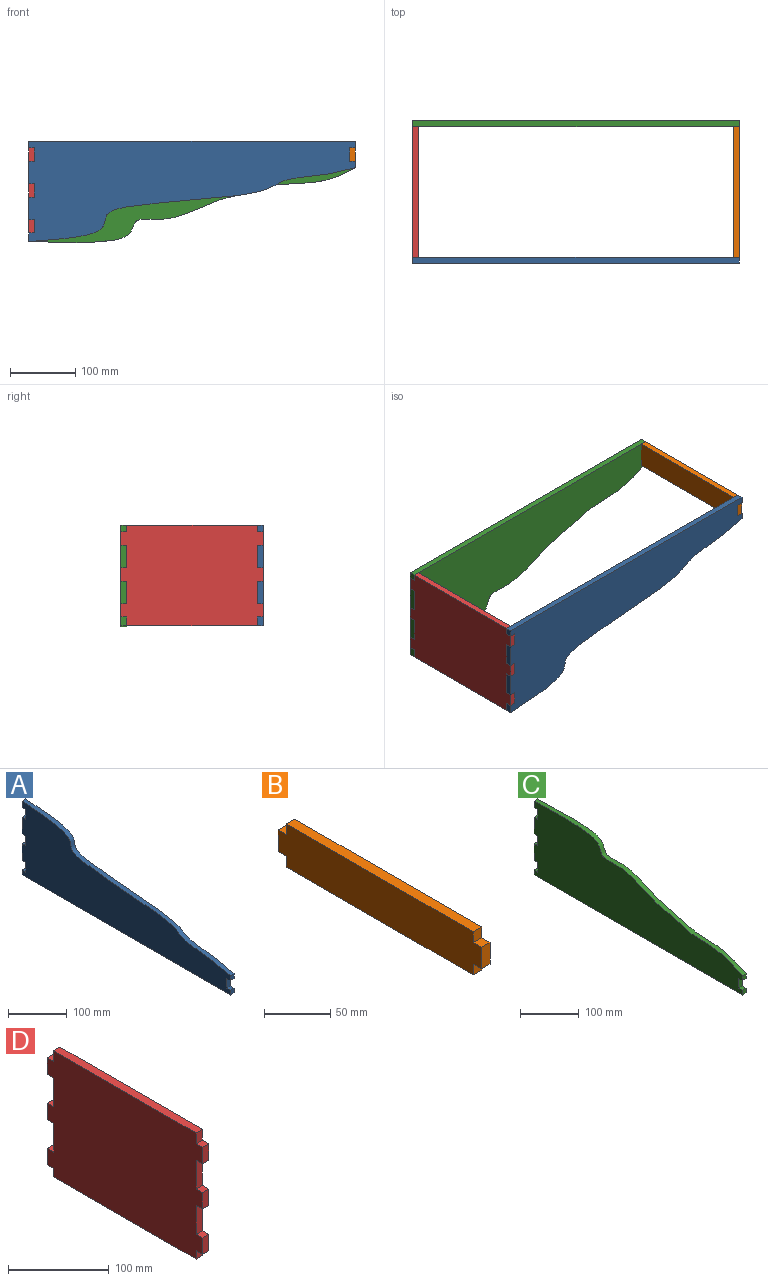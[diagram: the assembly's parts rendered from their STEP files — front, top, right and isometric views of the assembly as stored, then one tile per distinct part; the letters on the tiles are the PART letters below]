
ASSEMBLY  parts=4 mates=3
PART A: 22 faces, bbox 9x500x153.2 mm
  f0: plane 10x9mm, normal (0,1,0), area 90mm2, adj f1,f19,f20,f21
  f1: plane 9x9mm, normal (0,0,1), area 81mm2, adj f0,f2,f20,f21
  f2: plane 20x9mm, normal (0,1,0), area 180mm2, adj f1,f3,f20,f21
  f3: plane 9x9mm, normal (0,0,-1), area 81mm2, adj f2,f4,f20,f21
  f4: plane 35x9mm, normal (0,1,0), area 315mm2, adj f3,f5,f20,f21
  f5: plane 9x9mm, normal (0,0,1), area 81mm2, adj f4,f6,f20,f21
  f6: plane 20x9mm, normal (0,1,0), area 180mm2, adj f5,f7,f20,f21
  f7: plane 9x9mm, normal (0,0,-1), area 81mm2, adj f6,f8,f20,f21
  f8: plane 35x9mm, normal (0,1,0), area 315mm2, adj f7,f9,f20,f21
  f9: plane 9x9mm, normal (0,0,1), area 81mm2, adj f8,f10,f20,f21
  f10: plane 20x9mm, normal (0,1,0), area 180mm2, adj f9,f11,f20,f21
  f11: plane 9x9mm, normal (0,0,-1), area 81mm2, adj f10,f12,f20,f21
  f12: plane 13.18x9mm, normal (0,1,0), area 118.6mm2, adj f11,f13,f20,f21
  f13: extruded ~500x113.18mm, area 4761mm2, adj f12,f14,f20,f21
  f14: plane 10x9mm, normal (0,-1,0), area 90mm2, adj f13,f15,f20,f21
  f15: plane 9x9mm, normal (0,0,-1), area 81mm2, adj f14,f16,f20,f21
  f16: plane 20x9mm, normal (0,-1,0), area 180mm2, adj f15,f17,f20,f21
  f17: plane 9x9mm, normal (0,0,1), area 81mm2, adj f16,f18,f20,f21
  f18: plane 10x9mm, normal (0,-1,0), area 90mm2, adj f17,f19,f20,f21
  f19: plane 500x9mm, normal (0,0,-1), area 4500mm2, adj f0,f18,f20,f21
  f20: plane 500x153.18mm, normal (1,0,0), area 46145.7mm2, adj f0,f1,f2,f3,f4,f5,f6,f7
  f21: plane 500x153.18mm, normal (-1,0,0), area 46145.7mm2, adj f0,f1,f2,f3,f4,f5,f6,f7
PART B: 14 faces, bbox 9x218x40 mm
  f0: plane 9x9mm, normal (0,0,1), area 81mm2, adj f1,f11,f12,f13
  f1: plane 10x9mm, normal (0,1,0), area 90mm2, adj f0,f2,f12,f13
  f2: plane 200x9mm, normal (0,0,1), area 1800mm2, adj f1,f3,f12,f13
  f3: plane 10x9mm, normal (0,-1,0), area 90mm2, adj f2,f4,f12,f13
  f4: plane 9x9mm, normal (0,0,1), area 81mm2, adj f3,f5,f12,f13
  f5: plane 20x9mm, normal (0,-1,0), area 180mm2, adj f4,f6,f12,f13
  f6: plane 9x9mm, normal (0,0,-1), area 81mm2, adj f5,f7,f12,f13
  f7: plane 10x9mm, normal (0,-1,0), area 90mm2, adj f6,f8,f12,f13
  f8: plane 200x9mm, normal (0,0,-1), area 1800mm2, adj f7,f9,f12,f13
  f9: plane 10x9mm, normal (0,1,0), area 90mm2, adj f8,f10,f12,f13
  f10: plane 9x9mm, normal (0,0,-1), area 81mm2, adj f9,f11,f12,f13
  f11: plane 20x9mm, normal (0,1,0), area 180mm2, adj f0,f10,f12,f13
  f12: plane 218x40mm, normal (1,0,0), area 8360mm2, adj f0,f1,f2,f3,f4,f5,f6,f7
  f13: plane 218x40mm, normal (-1,0,0), area 8360mm2, adj f0,f1,f2,f3,f4,f5,f6,f7
PART C: 22 faces, bbox 9x500x159.2 mm
  f0: plane 10x9mm, normal (0,1,0), area 90mm2, adj f1,f19,f20,f21
  f1: plane 9x9mm, normal (0,0,1), area 81mm2, adj f0,f2,f20,f21
  f2: plane 20x9mm, normal (0,1,0), area 180mm2, adj f1,f3,f20,f21
  f3: plane 9x9mm, normal (0,0,-1), area 81mm2, adj f2,f4,f20,f21
  f4: plane 35x9mm, normal (0,1,0), area 315mm2, adj f3,f5,f20,f21
  f5: plane 9x9mm, normal (0,0,1), area 81mm2, adj f4,f6,f20,f21
  f6: plane 20x9mm, normal (0,1,0), area 180mm2, adj f5,f7,f20,f21
  f7: plane 9x9mm, normal (0,0,-1), area 81mm2, adj f6,f8,f20,f21
  f8: plane 35x9mm, normal (0,1,0), area 315mm2, adj f7,f9,f20,f21
  f9: plane 9x9mm, normal (0,0,1), area 81mm2, adj f8,f10,f20,f21
  f10: plane 20x9mm, normal (0,1,0), area 180mm2, adj f9,f11,f20,f21
  f11: plane 9x9mm, normal (0,0,-1), area 81mm2, adj f10,f12,f20,f21
  f12: plane 13.18x9mm, normal (0,1,0), area 118.6mm2, adj f11,f13,f20,f21
  f13: extruded ~500x114.61mm, area 4761mm2, adj f12,f14,f20,f21
  f14: plane 10x9mm, normal (0,-1,0), area 90mm2, adj f13,f15,f20,f21
  f15: plane 9x9mm, normal (0,0,-1), area 81mm2, adj f14,f16,f20,f21
  f16: plane 20x9mm, normal (0,-1,0), area 180mm2, adj f15,f17,f20,f21
  f17: plane 9x9mm, normal (0,0,1), area 81mm2, adj f16,f18,f20,f21
  f18: plane 10x9mm, normal (0,-1,0), area 90mm2, adj f17,f19,f20,f21
  f19: plane 500x9mm, normal (0,0,-1), area 4500mm2, adj f0,f18,f20,f21
  f20: plane 500x159.23mm, normal (1,0,0), area 52130.7mm2, adj f0,f1,f2,f3,f4,f5,f6,f7
  f21: plane 500x159.23mm, normal (-1,0,0), area 52130.7mm2, adj f0,f1,f2,f3,f4,f5,f6,f7
PART D: 30 faces, bbox 9x218x153.2 mm
  f0: plane 35x9mm, normal (0,1,0), area 315mm2, adj f1,f27,f28,f29
  f1: plane 9x9mm, normal (0,0,-1), area 81mm2, adj f0,f2,f28,f29
  f2: plane 20x9mm, normal (0,1,0), area 180mm2, adj f1,f3,f28,f29
  f3: plane 9x9mm, normal (0,0,1), area 81mm2, adj f2,f4,f28,f29
  f4: plane 35x9mm, normal (0,1,0), area 315mm2, adj f3,f5,f28,f29
  f5: plane 9x9mm, normal (0,0,-1), area 81mm2, adj f4,f6,f28,f29
  f6: plane 20x9mm, normal (0,1,0), area 180mm2, adj f5,f7,f28,f29
  f7: plane 9x9mm, normal (0,0,1), area 81mm2, adj f6,f8,f28,f29
  f8: plane 13.18x9mm, normal (0,1,0), area 118.6mm2, adj f7,f9,f28,f29
  f9: plane 200x9mm, normal (0,0,1), area 1800mm2, adj f8,f10,f28,f29
  f10: plane 13.18x9mm, normal (0,-1,0), area 118.6mm2, adj f9,f11,f28,f29
  f11: plane 9x9mm, normal (0,0,1), area 81mm2, adj f10,f12,f28,f29
  f12: plane 20x9mm, normal (0,-1,0), area 180mm2, adj f11,f13,f28,f29
  f13: plane 9x9mm, normal (0,0,-1), area 81mm2, adj f12,f14,f28,f29
  f14: plane 35x9mm, normal (0,-1,0), area 315mm2, adj f13,f15,f28,f29
  f15: plane 9x9mm, normal (0,0,1), area 81mm2, adj f14,f16,f28,f29
  f16: plane 20x9mm, normal (0,-1,0), area 180mm2, adj f15,f17,f28,f29
  f17: plane 9x9mm, normal (0,0,-1), area 81mm2, adj f16,f18,f28,f29
  f18: plane 35x9mm, normal (0,-1,0), area 315mm2, adj f17,f19,f28,f29
  f19: plane 9x9mm, normal (0,0,1), area 81mm2, adj f18,f20,f28,f29
  f20: plane 20x9mm, normal (0,-1,0), area 180mm2, adj f19,f21,f28,f29
  f21: plane 9x9mm, normal (0,0,-1), area 81mm2, adj f20,f22,f28,f29
  f22: plane 10x9mm, normal (0,-1,0), area 90mm2, adj f21,f23,f28,f29
  f23: plane 200x9mm, normal (0,0,-1), area 1800mm2, adj f22,f24,f28,f29
  f24: plane 10x9mm, normal (0,1,0), area 90mm2, adj f23,f25,f28,f29
  f25: plane 9x9mm, normal (0,0,-1), area 81mm2, adj f24,f26,f28,f29
  f26: plane 20x9mm, normal (0,1,0), area 180mm2, adj f25,f27,f28,f29
  f27: plane 9x9mm, normal (0,0,1), area 81mm2, adj f0,f26,f28,f29
  f28: plane 218x153.18mm, normal (1,0,0), area 31716.3mm2, adj f0,f1,f2,f3,f4,f5,f6,f7
  f29: plane 218x153.18mm, normal (-1,0,0), area 31716.3mm2, adj f0,f1,f2,f3,f4,f5,f6,f7
PLACE A rot(axis=(0.71,-0.71,0),180deg) t=(548.07,510.81,171.22)mm
PLACE B t=(789.07,610.81,171.22)mm
PLACE C rot(axis=(0.71,-0.71,0),180deg) t=(657.17,719.81,141.64)mm
PLACE D rot(axis=(0,1,0),180deg) t=(307.07,610.81,171.22)mm
MATE fastened D.f11 <-> A.f11  axis (0,0,-1) through (302.57,506.31,51.22)mm
MATE fastened B.f4 <-> A.f17  axis (0,0,1) through (793.57,506.31,181.22)mm
MATE fastened B.f0 <-> C.f17  axis (0,0,1) through (793.57,715.31,181.22)mm
